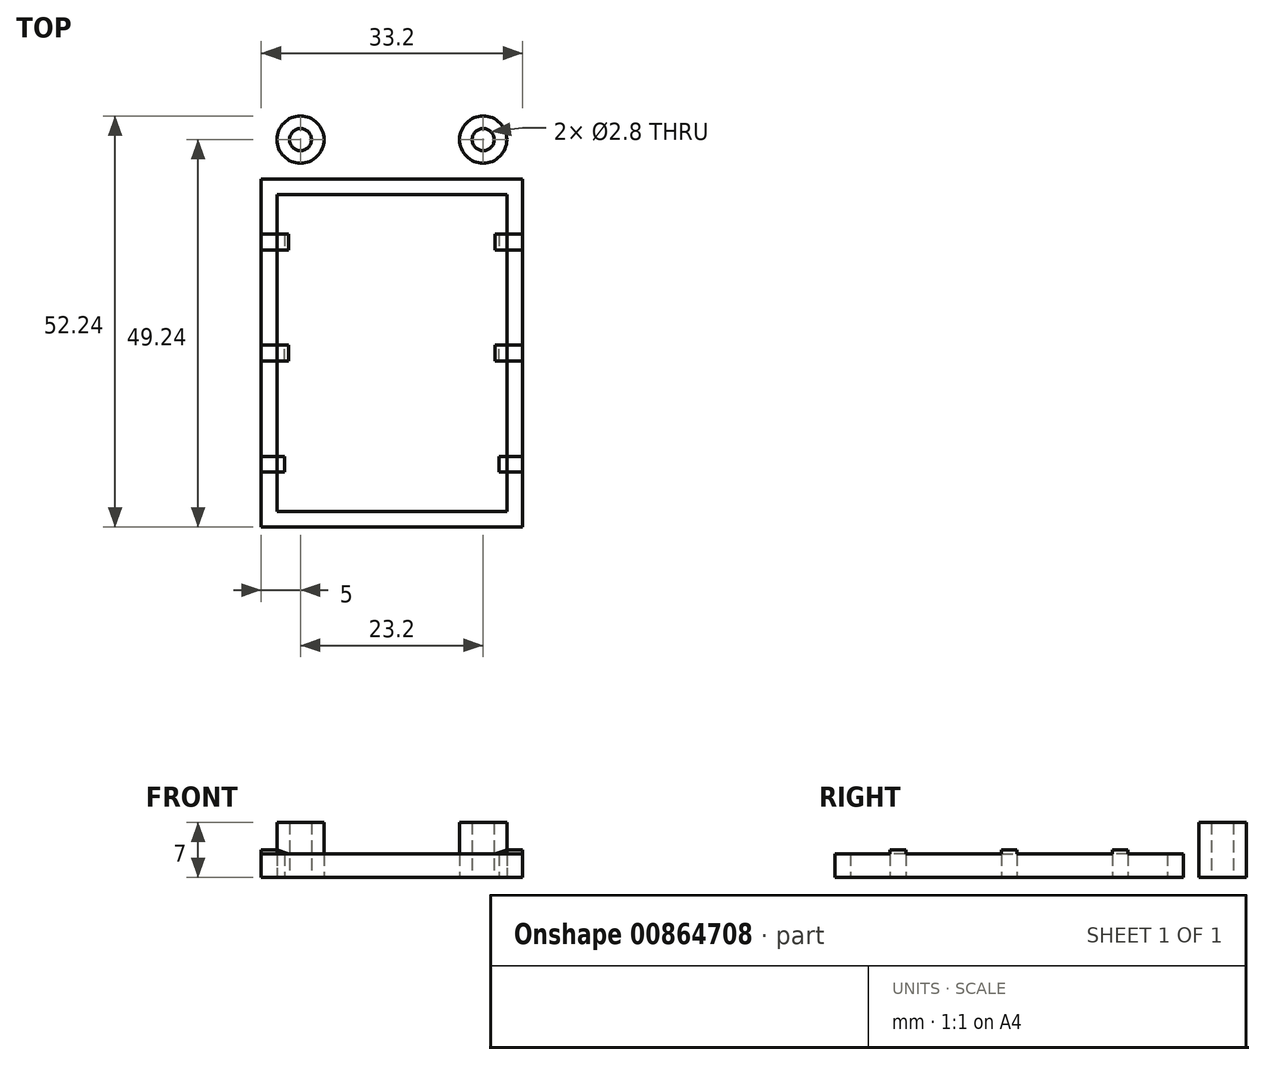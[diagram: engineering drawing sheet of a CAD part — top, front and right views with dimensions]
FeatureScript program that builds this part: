
annotation { "Feature Type Name" : "Feature", "Feature Type Description" : "" }
export const myFeature = defineFeature(function(context is Context, id is Id, definition is map)
    precondition{}
    {
        {
            var Q0;
            Q0=qCreatedBy(makeId("Top.planeOp"),FACE);
            var sketch = newSketch(context, id + "F0", { "sketchPlane" : qUnion([Q0])});
            skLineSegment(sketch, "E0.bottom", {"start": v(0, 0) * mm, "end": v(29.2, 0) * mm});
            skLineSegment(sketch, "E0.top", {"start": v(0, 40.24) * mm, "end": v(29.2, 40.24) * mm});
            skLineSegment(sketch, "E0.left", {"start": v(0, 0) * mm, "end": v(0, 40.24) * mm});
            skLineSegment(sketch, "E0.right", {"start": v(29.2, 0) * mm, "end": v(29.2, 40.24) * mm});
            skLineSegment(sketch, "E1.bottom", {"start": v(0, 35.24) * mm, "end": v(1, 35.24) * mm});
            skLineSegment(sketch, "E1.top", {"start": v(0, 33.24) * mm, "end": v(1, 33.24) * mm});
            skLineSegment(sketch, "E1.left", {"start": v(0, 35.24) * mm, "end": v(0, 33.24) * mm});
            skLineSegment(sketch, "E1.right", {"start": v(1, 35.24) * mm, "end": v(1, 33.24) * mm});
            skLineSegment(sketch, "E2.bottom", {"start": v(0, 19.12) * mm, "end": v(1, 19.12) * mm});
            skLineSegment(sketch, "E2.top", {"start": v(0, 21.12) * mm, "end": v(1, 21.12) * mm});
            skLineSegment(sketch, "E2.left", {"start": v(0, 19.12) * mm, "end": v(0, 21.12) * mm});
            skLineSegment(sketch, "E2.right", {"start": v(1, 19.12) * mm, "end": v(1, 21.12) * mm});
            skLineSegment(sketch, "E3.bottom", {"start": v(0, 5) * mm, "end": v(1, 5) * mm});
            skLineSegment(sketch, "E3.top", {"start": v(0, 7) * mm, "end": v(1, 7) * mm});
            skLineSegment(sketch, "E3.left", {"start": v(0, 5) * mm, "end": v(0, 7) * mm});
            skLineSegment(sketch, "E3.right", {"start": v(1, 5) * mm, "end": v(1, 7) * mm});
            skLineSegment(sketch, "E4", {"start": v(1, 20.12) * mm, "end": v(0, 20.12) * mm, "construction": true});
            skLineSegment(sketch, "E5", {"start": v(14.6, 40.24) * mm, "end": v(14.6, 0) * mm, "construction": true});
            skLineSegment(sketch, "E6.MirrorCS", {"start": v(29.2, 21.12) * mm, "end": v(28.2, 21.12) * mm});
            skLineSegment(sketch, "E7.MirrorCS", {"start": v(29.2, 7) * mm, "end": v(28.2, 7) * mm});
            skLineSegment(sketch, "E8.MirrorCS", {"start": v(29.2, 33.24) * mm, "end": v(28.2, 33.24) * mm});
            skLineSegment(sketch, "E9.MirrorCS", {"start": v(29.2, 5) * mm, "end": v(28.2, 5) * mm});
            skLineSegment(sketch, "E10.MirrorCS", {"start": v(29.2, 35.24) * mm, "end": v(28.2, 35.24) * mm});
            skLineSegment(sketch, "E11.MirrorCS", {"start": v(29.2, 19.12) * mm, "end": v(28.2, 19.12) * mm});
            skLineSegment(sketch, "E12.MirrorCS", {"start": v(29.2, 19.12) * mm, "end": v(29.2, 21.12) * mm});
            skLineSegment(sketch, "E13.MirrorCS", {"start": v(28.2, 19.12) * mm, "end": v(28.2, 21.12) * mm});
            skLineSegment(sketch, "E14.MirrorCS", {"start": v(28.2, 20.12) * mm, "end": v(29.2, 20.12) * mm, "construction": true});
            skLineSegment(sketch, "E15.MirrorCS", {"start": v(29.2, 5) * mm, "end": v(29.2, 7) * mm});
            skLineSegment(sketch, "E16.MirrorCS", {"start": v(28.2, 5) * mm, "end": v(28.2, 7) * mm});
            skLineSegment(sketch, "E17.MirrorCS", {"start": v(29.2, 35.24) * mm, "end": v(29.2, 33.24) * mm});
            skLineSegment(sketch, "E18.MirrorCS", {"start": v(28.2, 35.24) * mm, "end": v(28.2, 33.24) * mm});
            skLineSegment(sketch, "E19.0", {"start": v(-2, 42.24) * mm, "end": v(31.2, 42.24) * mm});
            skLineSegment(sketch, "E19.1", {"start": v(-2, -2) * mm, "end": v(-2, 42.24) * mm});
            skLineSegment(sketch, "E19.2", {"start": v(-2, -2) * mm, "end": v(31.2, -2) * mm});
            skLineSegment(sketch, "E19.3", {"start": v(31.2, -2) * mm, "end": v(31.2, 42.24) * mm});
            skSolve(sketch);
        }
        {
            var Q0;
            {var subQ5=sQuery(id+"F0.wireOp",EDGE,"E0.bottom");Q0=makeQuery(id+"F0.imprint","IMPRINT",FACE,{"disambiguationData":[TD([[makeQuery(id+"F0.imprint","IMPRINT",EDGE,{"derivedFrom":subQ5}),-1.0]])]});}
            var Q1;
            Q1=makeQuery(id+"F0.imprint","IMPRINT",FACE,{"disambiguationData":[TD([[makeQuery(id+"F0.imprint","IMPRINT",EDGE,{"derivedFrom":sQuery(id+"F0.wireOp",EDGE,"E1.bottom")}),-1.0]])]});
            var Q2;
            Q2=makeQuery(id+"F0.imprint","IMPRINT",FACE,{"disambiguationData":[TD([[makeQuery(id+"F0.imprint","IMPRINT",EDGE,{"derivedFrom":sQuery(id+"F0.wireOp",EDGE,"E2.bottom")}),1.0]])]});
            var Q3;
            Q3=makeQuery(id+"F0.imprint","IMPRINT",FACE,{"disambiguationData":[TD([[makeQuery(id+"F0.imprint","IMPRINT",EDGE,{"derivedFrom":sQuery(id+"F0.wireOp",EDGE,"E3.bottom")}),1.0]])]});
            var Q4;
            Q4=makeQuery(id+"F0.imprint","IMPRINT",FACE,{"disambiguationData":[TD([[makeQuery(id+"F0.imprint","IMPRINT",EDGE,{"derivedFrom":sQuery(id+"F0.wireOp",EDGE,"E7.MirrorCS")}),1.0]])]});
            var Q5;
            Q5=makeQuery(id+"F0.imprint","IMPRINT",FACE,{"disambiguationData":[TD([[makeQuery(id+"F0.imprint","IMPRINT",EDGE,{"derivedFrom":sQuery(id+"F0.wireOp",EDGE,"E6.MirrorCS")}),1.0]])]});
            var Q6;
            Q6=makeQuery(id+"F0.imprint","IMPRINT",FACE,{"disambiguationData":[TD([[makeQuery(id+"F0.imprint","IMPRINT",EDGE,{"derivedFrom":sQuery(id+"F0.wireOp",EDGE,"E8.MirrorCS")}),-1.0]])]});
            extrude(context, id + "F1", {"entities" : qUnion([Q0, Q1, Q2, Q3, Q4, Q5, Q6]), "depth" : 3 * mm, "offsetDistance" : 25 * mm});
        }
        {
            var Q0;
            Q0=makeQuery(id+"F1.opExtrude","SWEPT_FACE",FACE,{"disambiguationData":[OSD([sQuery(id+"F0.wireOp",EDGE,"E9.MirrorCS")])]});
            var sketch = newSketch(context, id + "F2", { "sketchPlane" : qUnion([Q0])});
            skLineSegment(sketch, "E20.0", {"start": v(28.2, 3) * mm, "end": v(28.2, 0) * mm});
            skLineSegment(sketch, "E21.0", {"start": v(1, 3) * mm, "end": v(1, 0) * mm});
            skLineSegment(sketch, "E22.0", {"start": v(0, 3) * mm, "end": v(1, 3) * mm});
            skLineSegment(sketch, "E23.0", {"start": v(-2, 3) * mm, "end": v(31.2, 3) * mm});
            skLineSegment(sketch, "E24.0", {"start": v(29.2, 3) * mm, "end": v(29.2, 0) * mm});
            skLineSegment(sketch, "E25.0", {"start": v(0, 3) * mm, "end": v(0, 0) * mm});
            skLineSegment(sketch, "E26", {"start": v(1, 3) * mm, "end": v(1.5, 3) * mm});
            skLineSegment(sketch, "E27", {"start": v(1.5, 3) * mm, "end": v(0, 3.5) * mm});
            skLineSegment(sketch, "E28", {"start": v(0, 3.5) * mm, "end": v(0, 3) * mm});
            skLineSegment(sketch, "E29", {"start": v(28.2, 3) * mm, "end": v(27.7, 3) * mm});
            skLineSegment(sketch, "E30", {"start": v(27.7, 3) * mm, "end": v(29.2, 3.5) * mm});
            skLineSegment(sketch, "E31", {"start": v(29.2, 3.5) * mm, "end": v(29.2, 3) * mm});
            skLineSegment(sketch, "E32", {"start": v(0, 3.5) * mm, "end": v(-2, 3.5) * mm});
            skLineSegment(sketch, "E33", {"start": v(-2, 3.5) * mm, "end": v(-2, 3) * mm});
            skLineSegment(sketch, "E34", {"start": v(29.2, 3.5) * mm, "end": v(31.2, 3.5) * mm});
            skLineSegment(sketch, "E35", {"start": v(31.2, 3.5) * mm, "end": v(31.2, 3) * mm});
            skSolve(sketch);
        }
        {
            var Q0;
            {var subQ2=sQuery(id+"F2.wireOp",EDGE,"E29");Q0=makeQuery(id+"F2.imprint","IMPRINT",FACE,{"disambiguationData":[TD([[makeQuery(id+"F2.imprint","IMPRINT",EDGE,{"derivedFrom":subQ2}),-1.0]])]});}
            var Q1;
            {var subQ0=sQuery(id+"F2.wireOp",EDGE,"E31");Q1=makeQuery(id+"F2.imprint","IMPRINT",FACE,{"disambiguationData":[TD([[makeQuery(id+"F2.imprint","IMPRINT",EDGE,{"derivedFrom":subQ0}),1.0]])]});}
            var Q2;
            {var subQ0=sQuery(id+"F2.wireOp",EDGE,"E26");Q2=makeQuery(id+"F2.imprint","IMPRINT",FACE,{"disambiguationData":[TD([[makeQuery(id+"F2.imprint","IMPRINT",EDGE,{"derivedFrom":subQ0}),1.0]])]});}
            var Q3;
            {var subQ2=sQuery(id+"F2.wireOp",EDGE,"E28");Q3=makeQuery(id+"F2.imprint","IMPRINT",FACE,{"disambiguationData":[TD([[makeQuery(id+"F2.imprint","IMPRINT",EDGE,{"derivedFrom":subQ2}),-1.0]])]});}
            var Q4;
            Q4=makeQuery(id+"F1.opExtrude","SWEPT_FACE",FACE,{"disambiguationData":[OSD([sQuery(id+"F0.wireOp",EDGE,"E3.top")])]});
            extrude(context, id + "F3", {"entities" : qUnion([Q0, Q1, Q2, Q3]), "operationType" : NewBodyOperationType.ADD, "endBound" : BoundingType.UP_TO_SURFACE, "oppositeDirection" : true, "depth" : 25 * mm, "endBoundEntityFace" : qUnion([Q4]), "offsetDistance" : 25 * mm});
        }
        {
            var Q0;
            Q0=makeQuery(id+"F1.opExtrude","SWEPT_FACE",FACE,{"disambiguationData":[OSD([sQuery(id+"F0.wireOp",EDGE,"E2.bottom")])]});
            var sketch = newSketch(context, id + "F4", { "sketchPlane" : qUnion([Q0])});
            skLineSegment(sketch, "E36.0.0", {"start": v(0, 0) * mm, "end": v(1, 0) * mm});
            skLineSegment(sketch, "E36.0.1", {"start": v(1, 0) * mm, "end": v(1, 3) * mm});
            skLineSegment(sketch, "E36.0.2", {"start": v(1, 3) * mm, "end": v(1.5, 3) * mm});
            skLineSegment(sketch, "E36.0.3", {"start": v(1.5, 3) * mm, "end": v(0, 3.5) * mm});
            skLineSegment(sketch, "E36.0.4", {"start": v(0, 3.5) * mm, "end": v(-2, 3.5) * mm});
            skLineSegment(sketch, "E36.0.5", {"start": v(-2, 3.5) * mm, "end": v(-2, 3) * mm});
            skLineSegment(sketch, "E36.0.6", {"start": v(-2, 3) * mm, "end": v(0, 3) * mm});
            skLineSegment(sketch, "E36.0.7", {"start": v(0, 3) * mm, "end": v(0, 0) * mm});
            skLineSegment(sketch, "E37.0.0", {"start": v(28.2, 0) * mm, "end": v(29.2, 0) * mm});
            skLineSegment(sketch, "E37.0.1", {"start": v(29.2, 0) * mm, "end": v(29.2, 3) * mm});
            skLineSegment(sketch, "E37.0.2", {"start": v(29.2, 3) * mm, "end": v(31.2, 3) * mm});
            skLineSegment(sketch, "E37.0.3", {"start": v(31.2, 3) * mm, "end": v(31.2, 3.5) * mm});
            skLineSegment(sketch, "E37.0.4", {"start": v(31.2, 3.5) * mm, "end": v(29.2, 3.5) * mm});
            skLineSegment(sketch, "E37.0.5", {"start": v(29.2, 3.5) * mm, "end": v(27.7, 3) * mm});
            skLineSegment(sketch, "E37.0.6", {"start": v(27.7, 3) * mm, "end": v(28.2, 3) * mm});
            skLineSegment(sketch, "E37.0.7", {"start": v(28.2, 3) * mm, "end": v(28.2, 0) * mm});
            skSolve(sketch);
        }
        {
            var Q0;
            Q0=makeQuery(id+"F4.imprint","IMPRINT",FACE,{"disambiguationData":[TD([[makeQuery(id+"F4.imprint","IMPRINT",EDGE,{"derivedFrom":sQuery(id+"F4.wireOp",EDGE,"E37.0.0")}),1.0]])]});
            var Q1;
            Q1=makeQuery(id+"F4.imprint","IMPRINT",FACE,{"disambiguationData":[TD([[makeQuery(id+"F4.imprint","IMPRINT",EDGE,{"derivedFrom":sQuery(id+"F4.wireOp",EDGE,"E36.0.2")}),1.0]])]});
            var Q2;
            Q2=makeQuery(id+"F1.opExtrude","SWEPT_FACE",FACE,{"disambiguationData":[OSD([sQuery(id+"F0.wireOp",EDGE,"E2.top")])]});
            extrude(context, id + "F5", {"entities" : qUnion([Q0, Q1]), "operationType" : NewBodyOperationType.ADD, "endBound" : BoundingType.UP_TO_SURFACE, "oppositeDirection" : true, "depth" : 25 * mm, "endBoundEntityFace" : qUnion([Q2]), "offsetDistance" : 25 * mm});
        }
        {
            var Q0;
            Q0=makeQuery(id+"F1.opExtrude","SWEPT_FACE",FACE,{"disambiguationData":[OSD([sQuery(id+"F0.wireOp",EDGE,"E1.top")])]});
            var sketch = newSketch(context, id + "F6", { "sketchPlane" : qUnion([Q0])});
            skLineSegment(sketch, "E38.0.0", {"start": v(0, 0) * mm, "end": v(1, 0) * mm});
            skLineSegment(sketch, "E38.0.1", {"start": v(1, 0) * mm, "end": v(1, 3) * mm});
            skLineSegment(sketch, "E38.0.2", {"start": v(1, 3) * mm, "end": v(1.5, 3) * mm});
            skLineSegment(sketch, "E38.0.3", {"start": v(1.5, 3) * mm, "end": v(0, 3.5) * mm});
            skLineSegment(sketch, "E38.0.4", {"start": v(0, 3.5) * mm, "end": v(-2, 3.5) * mm});
            skLineSegment(sketch, "E38.0.5", {"start": v(-2, 3.5) * mm, "end": v(-2, 3) * mm});
            skLineSegment(sketch, "E38.0.6", {"start": v(-2, 3) * mm, "end": v(0, 3) * mm});
            skLineSegment(sketch, "E38.0.7", {"start": v(0, 3) * mm, "end": v(0, 0) * mm});
            skLineSegment(sketch, "E39.0.0", {"start": v(28.2, 0) * mm, "end": v(29.2, 0) * mm});
            skLineSegment(sketch, "E39.0.1", {"start": v(29.2, 0) * mm, "end": v(29.2, 3) * mm});
            skLineSegment(sketch, "E39.0.2", {"start": v(29.2, 3) * mm, "end": v(31.2, 3) * mm});
            skLineSegment(sketch, "E39.0.3", {"start": v(31.2, 3) * mm, "end": v(31.2, 3.5) * mm});
            skLineSegment(sketch, "E39.0.4", {"start": v(31.2, 3.5) * mm, "end": v(29.2, 3.5) * mm});
            skLineSegment(sketch, "E39.0.5", {"start": v(29.2, 3.5) * mm, "end": v(27.7, 3) * mm});
            skLineSegment(sketch, "E39.0.6", {"start": v(27.7, 3) * mm, "end": v(28.2, 3) * mm});
            skLineSegment(sketch, "E39.0.7", {"start": v(28.2, 3) * mm, "end": v(28.2, 0) * mm});
            skSolve(sketch);
        }
        {
            var Q0;
            Q0=makeQuery(id+"F6.imprint","IMPRINT",FACE,{"disambiguationData":[TD([[makeQuery(id+"F6.imprint","IMPRINT",EDGE,{"derivedFrom":sQuery(id+"F6.wireOp",EDGE,"E38.0.2")}),1.0]])]});
            var Q1;
            Q1=makeQuery(id+"F6.imprint","IMPRINT",FACE,{"disambiguationData":[TD([[makeQuery(id+"F6.imprint","IMPRINT",EDGE,{"derivedFrom":sQuery(id+"F6.wireOp",EDGE,"E39.0.0")}),1.0]])]});
            var Q2;
            Q2=makeQuery(id+"F1.opExtrude","SWEPT_FACE",FACE,{"disambiguationData":[OSD([sQuery(id+"F0.wireOp",EDGE,"E1.bottom")])]});
            extrude(context, id + "F7", {"entities" : qUnion([Q0, Q1]), "operationType" : NewBodyOperationType.ADD, "endBound" : BoundingType.UP_TO_SURFACE, "oppositeDirection" : true, "depth" : 25 * mm, "endBoundEntityFace" : qUnion([Q2]), "offsetDistance" : 25 * mm});
        }
        {
            var Q0;
            Q0=qCreatedBy(makeId("Top.planeOp"),FACE);
            var sketch = newSketch(context, id + "F8", { "sketchPlane" : qUnion([Q0])});
            skLineSegment(sketch, "E40.0", {"start": v(-2, 42.24) * mm, "end": v(31.2, 42.24) * mm});
            skCircle(sketch, "E41", {"center": v(26.2, 47.24) * mm, "radius": 1.4 * mm});
            skCircle(sketch, "E42", {"center": v(3, 47.24) * mm, "radius": 1.4 * mm});
            skLineSegment(sketch, "E43.0", {"start": v(-2, -2) * mm, "end": v(-2, 42.24) * mm});
            skLineSegment(sketch, "E44.0", {"start": v(31.2, -2) * mm, "end": v(31.2, 42.24) * mm});
            skLineSegment(sketch, "E45", {"start": v(31.2, 20.12) * mm, "end": v(-2, 20.12) * mm});
            skCircle(sketch, "E46", {"center": v(3, 47.24) * mm, "radius": 3 * mm});
            skCircle(sketch, "E47", {"center": v(26.2, 47.24) * mm, "radius": 3 * mm});
            skCircle(sketch, "E48.MirrorC", {"center": v(3, -7) * mm, "radius": 3 * mm});
            skCircle(sketch, "E49.MirrorC", {"center": v(26.2, -7) * mm, "radius": 3 * mm});
            skCircle(sketch, "E50.MirrorC", {"center": v(26.2, -7) * mm, "radius": 1.4 * mm});
            skCircle(sketch, "E51.MirrorC", {"center": v(3, -7) * mm, "radius": 1.4 * mm});
            skSolve(sketch);
        }
        {
            var Q0;
            Q0=makeQuery(id+"F8.imprint","IMPRINT",FACE,{"disambiguationData":[TD([[makeQuery(id+"F8.imprint","IMPRINT",EDGE,{"derivedFrom":sQuery(id+"F8.wireOp",EDGE,"E42")}),-1.0]])]});
            var Q1;
            Q1=makeQuery(id+"F8.imprint","IMPRINT",FACE,{"disambiguationData":[TD([[makeQuery(id+"F8.imprint","IMPRINT",EDGE,{"derivedFrom":sQuery(id+"F8.wireOp",EDGE,"E41")}),-1.0]])]});
            var Q2;
            Q2=makeQuery(id+"F8.imprint","IMPRINT",FACE,{"disambiguationData":[TD([[makeQuery(id+"F8.imprint","IMPRINT",EDGE,{"derivedFrom":sQuery(id+"F8.wireOp",EDGE,"E48.MirrorC")}),-1.0]])]});
            var Q3;
            Q3=makeQuery(id+"F8.imprint","IMPRINT",FACE,{"disambiguationData":[TD([[makeQuery(id+"F8.imprint","IMPRINT",EDGE,{"derivedFrom":sQuery(id+"F8.wireOp",EDGE,"E49.MirrorC")}),-1.0]])]});
            extrude(context, id + "F9", {"entities" : qUnion([Q0, Q1, Q2, Q3]), "depth" : 7 * mm, "offsetDistance" : 25 * mm});
        }
    });
